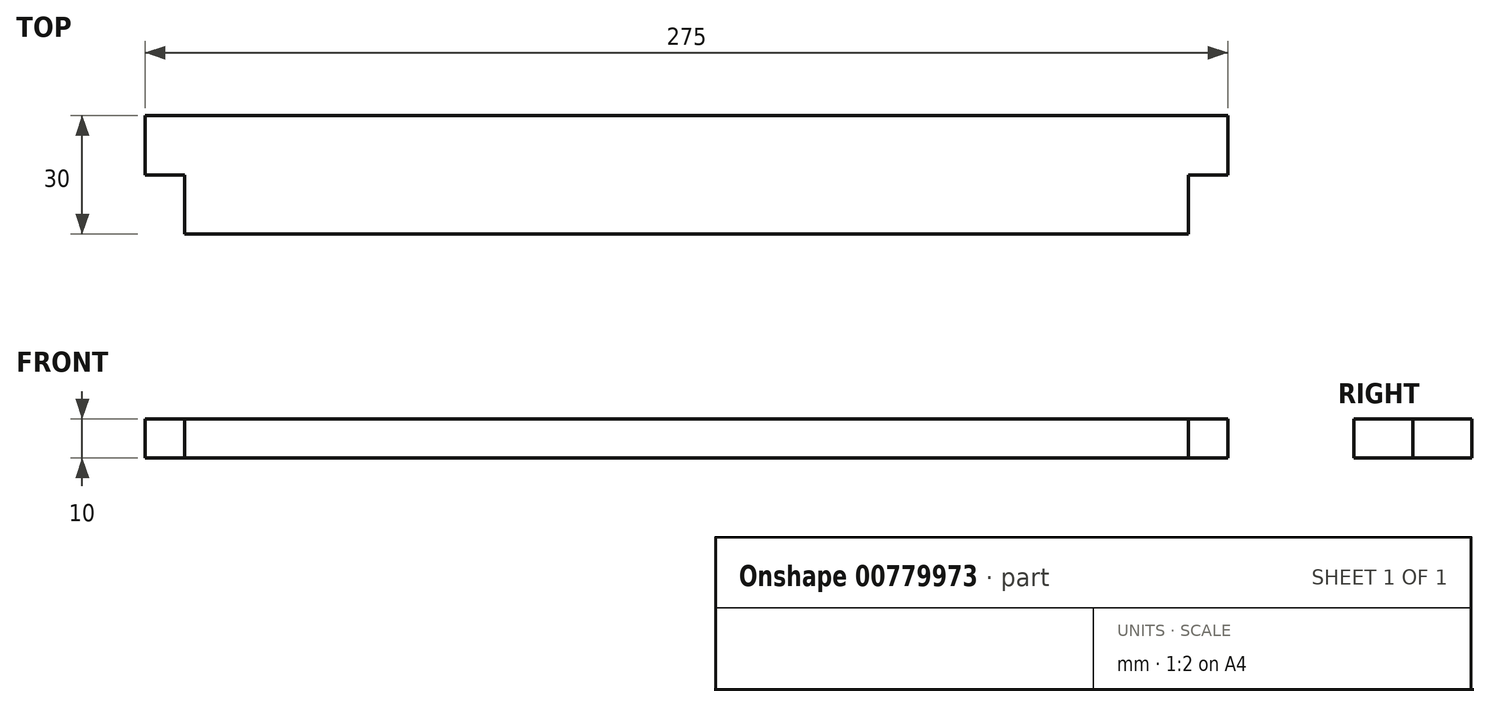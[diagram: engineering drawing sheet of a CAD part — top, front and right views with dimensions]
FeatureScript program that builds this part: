
annotation { "Feature Type Name" : "Feature", "Feature Type Description" : "" }
export const myFeature = defineFeature(function(context is Context, id is Id, definition is map)
    precondition{}
    {
        {
            var Q0;
            Q0=qCreatedBy(makeId("Top.planeOp"),FACE);
            var sketch = newSketch(context, id + "F0", { "sketchPlane" : qUnion([Q0])});
            skLineSegment(sketch, "E0", {"start": v(0, 0) * mm, "end": v(0, 30) * mm});
            skLineSegment(sketch, "E1", {"start": v(0, 30) * mm, "end": v(275, 30) * mm});
            skLineSegment(sketch, "E2", {"start": v(275, 30) * mm, "end": v(275, 0) * mm});
            skLineSegment(sketch, "E3", {"start": v(275, 0) * mm, "end": v(0, 0) * mm});
            skSolve(sketch);
        }
        {
            var Q0;
            Q0=qSketchRegion(id+"F0",true);
            extrude(context, id + "F1", {"entities" : qUnion([Q0]), "depth" : 10 * mm, "offsetDistance" : 25 * mm});
        }
        {
            var Q0;
            Q0=makeQuery(id+"F1.opExtrude","CAP_FACE",FACE,{"disambiguationData":[OSD([sQuery(id+"F0.wireOp",EDGE,"E0"),sQuery(id+"F0.wireOp",EDGE,"E1"),sQuery(id+"F0.wireOp",EDGE,"E2"),sQuery(id+"F0.wireOp",EDGE,"E3")])],"isStart":false});
            var sketch = newSketch(context, id + "F2", { "sketchPlane" : qUnion([Q0])});
            skLineSegment(sketch, "E4", {"start": v(0, 15) * mm, "end": v(10, 15) * mm});
            skLineSegment(sketch, "E5", {"start": v(10, 15) * mm, "end": v(10, 0) * mm});
            skLineSegment(sketch, "E6", {"start": v(10, 0) * mm, "end": v(0, 0) * mm});
            skLineSegment(sketch, "E7", {"start": v(275, 15) * mm, "end": v(265, 15) * mm});
            skLineSegment(sketch, "E8", {"start": v(265, 15) * mm, "end": v(265, 0) * mm});
            skLineSegment(sketch, "E9", {"start": v(265, 0) * mm, "end": v(275, 0) * mm});
            skLineSegment(sketch, "E10", {"start": v(0, 0) * mm, "end": v(0, 15) * mm});
            skLineSegment(sketch, "E11", {"start": v(275, 15) * mm, "end": v(275, 0) * mm});
            skSolve(sketch);
        }
        {
            var Q0;
            Q0=qSketchRegion(id+"F2",true);
            extrude(context, id + "F3", {"entities" : qUnion([Q0]), "operationType" : NewBodyOperationType.REMOVE, "endBound" : BoundingType.THROUGH_ALL, "oppositeDirection" : true, "depth" : 25 * mm, "offsetDistance" : 25 * mm});
        }
    });
